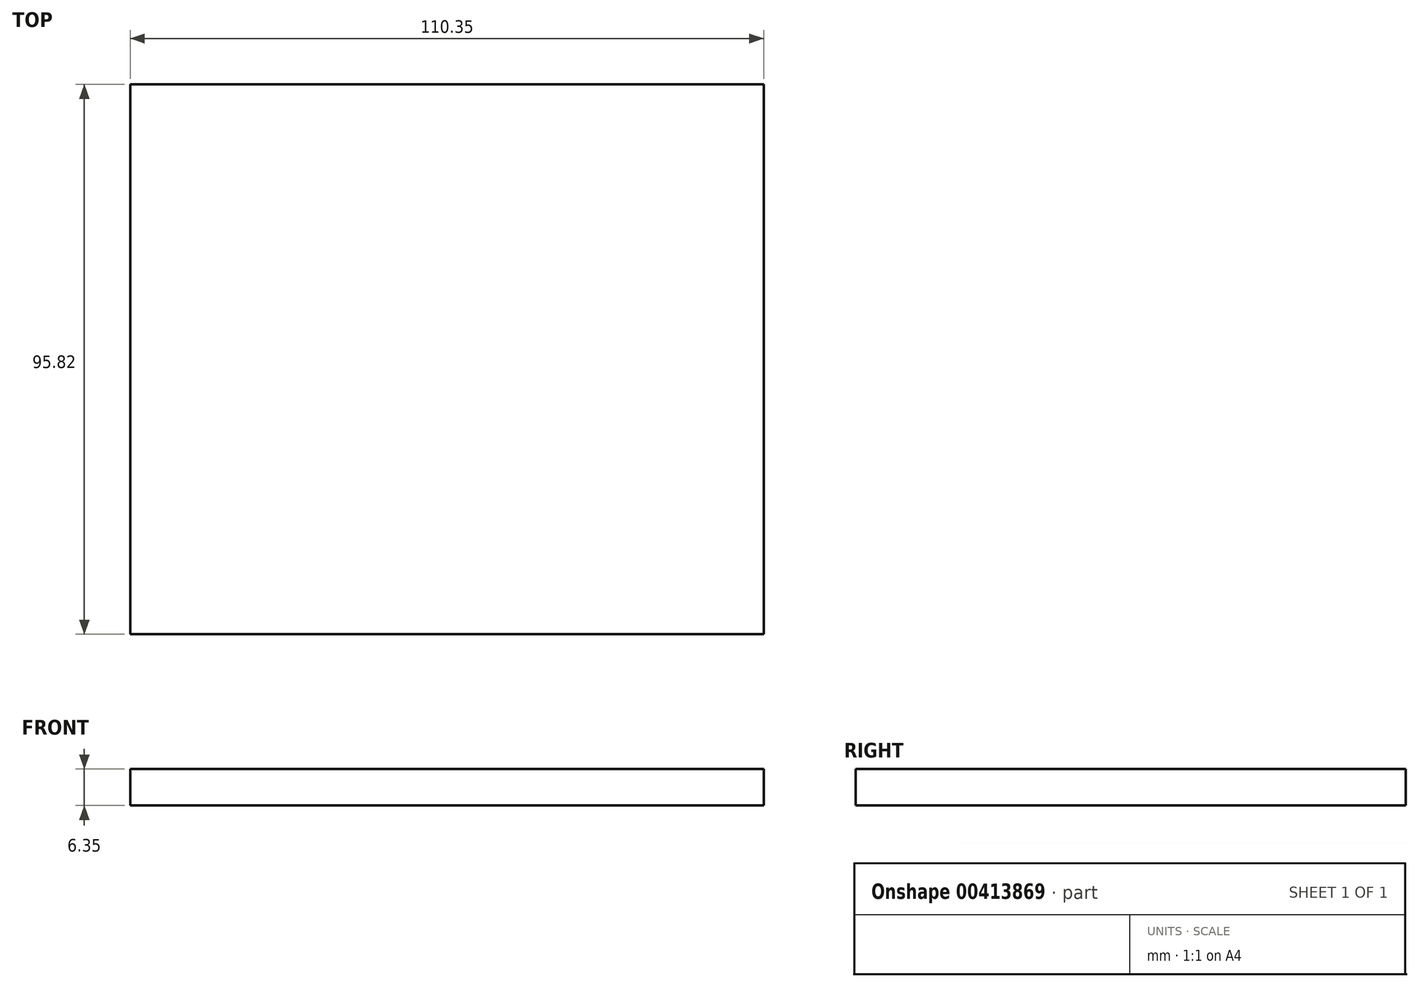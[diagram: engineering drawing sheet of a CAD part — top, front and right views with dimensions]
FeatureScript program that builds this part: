
annotation { "Feature Type Name" : "Feature", "Feature Type Description" : "" }
export const myFeature = defineFeature(function(context is Context, id is Id, definition is map)
    precondition{}
    {
        {
            var Q0;
            Q0=qCreatedBy(makeId("Top.planeOp"),FACE);
            var sketch = newSketch(context, id + "F0", { "sketchPlane" : qUnion([Q0])});
            skLineSegment(sketch, "E0.bottom", {"start": v(-57.74, 52.2) * mm, "end": v(52.6, 52.2) * mm});
            skLineSegment(sketch, "E0.top", {"start": v(-57.74, -43.63) * mm, "end": v(52.6, -43.63) * mm});
            skLineSegment(sketch, "E0.left", {"start": v(-57.74, 52.2) * mm, "end": v(-57.74, -43.63) * mm});
            skLineSegment(sketch, "E0.right", {"start": v(52.6, 52.2) * mm, "end": v(52.6, -43.63) * mm});
            skSolve(sketch);
        }
        {
            var Q0;
            Q0=sQuery(id+"F0.wireOp",EDGE,"E0.right");
            var Q1;
            Q1=sQuery(id+"F0.wireOp",EDGE,"E0.top");
            var Q2;
            Q2=sQuery(id+"F0.wireOp",EDGE,"E0.bottom");
            var Q3;
            Q3=sQuery(id+"F0.wireOp",EDGE,"E0.left");
            extrude(context, id + "F1", {"bodyType" : ToolBodyType.SURFACE, "surfaceEntities" : qUnion([Q0, Q1, Q2, Q3]), "depth" : 6.35 * mm});
        }
    });
